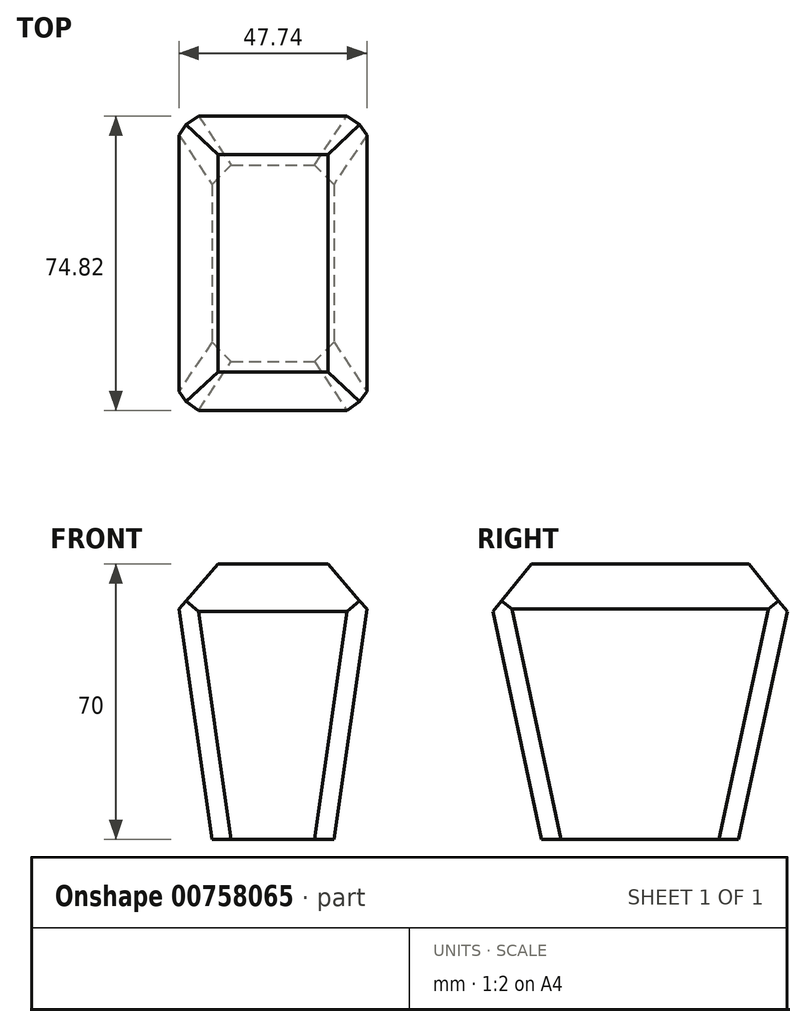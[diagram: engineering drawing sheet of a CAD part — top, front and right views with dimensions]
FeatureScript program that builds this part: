
annotation { "Feature Type Name" : "Feature", "Feature Type Description" : "" }
export const myFeature = defineFeature(function(context is Context, id is Id, definition is map)
    precondition{}
    {
        {
            var Q0;
            Q0=qCreatedBy(makeId("Top.planeOp"),FACE);
            cPlane(context, id + "F0", {"entities" : qUnion([Q0]), "cplaneType" : CPlaneType.OFFSET, "offset" : 70 * mm, "width" : 150 * mm, "height" : 150 * mm});
        }
        {
            var Q0;
            Q0=qCreatedBy(makeId("Top.planeOp"),FACE);
            var sketch = newSketch(context, id + "F1", { "sketchPlane" : qUnion([Q0])});
            skLineSegment(sketch, "E0.bottom", {"start": v(-15.5, 25) * mm, "end": v(15.5, 25) * mm});
            skLineSegment(sketch, "E0.top", {"start": v(-15.5, -25) * mm, "end": v(15.5, -25) * mm});
            skLineSegment(sketch, "E0.left", {"start": v(-15.5, 25) * mm, "end": v(-15.5, -25) * mm});
            skLineSegment(sketch, "E0.right", {"start": v(15.5, 25) * mm, "end": v(15.5, -25) * mm});
            skSolve(sketch);
        }
        {
            var Q0;
            Q0=qCreatedBy(id+"F0.planeOp",FACE);
            var sketch = newSketch(context, id + "F2", { "sketchPlane" : qUnion([Q0])});
            skLineSegment(sketch, "E1.bottom", {"start": v(-25.5, 40) * mm, "end": v(25.5, 40) * mm});
            skLineSegment(sketch, "E1.top", {"start": v(-25.5, -40) * mm, "end": v(25.5, -40) * mm});
            skLineSegment(sketch, "E1.left", {"start": v(-25.5, 40) * mm, "end": v(-25.5, -40) * mm});
            skLineSegment(sketch, "E1.right", {"start": v(25.5, 40) * mm, "end": v(25.5, -40) * mm});
            skSolve(sketch);
        }
        {
            var Q0;
            Q0=makeQuery(id+"F1.imprint","IMPRINT",FACE,{"disambiguationData":[TD([[makeQuery(id+"F1.imprint","IMPRINT",EDGE,{"derivedFrom":sQuery(id+"F1.wireOp",EDGE,"E0.bottom")}),-1.0]])]});
            var Q1;
            Q1=makeQuery(id+"F2.imprint","IMPRINT",FACE,{"disambiguationData":[TD([[makeQuery(id+"F2.imprint","IMPRINT",EDGE,{"derivedFrom":sQuery(id+"F2.wireOp",EDGE,"E1.bottom")}),-1.0]])]});
            loft(context, id + "F3", {"sheetProfilesArray" : [{ "sheetProfileEntities" : qUnion([Q0]) }, { "sheetProfileEntities" : qUnion([Q1]) }]});
        }
        {
            var Q0;
            Q0=makeQuery(id+"F3.opLoft","CAP_FACE",FACE,{"disambiguationData":[OSD([makeQuery(id+"F2.imprint","IMPRINT",FACE,{"disambiguationData":[TD([[makeQuery(id+"F2.imprint","IMPRINT",EDGE,{"derivedFrom":sQuery(id+"F2.wireOp",EDGE,"E1.bottom")}),-1.0]])]})])],"isStart":true});
            chamfer(context, id + "F4", {"entities" : qUnion([Q0]), "width" : 10 * mm, "tangentPropagation" : true});
        }
        {
            var Q0;
            Q0=makeQuery(id+"F3.opLoft","SWEPT_EDGE",EDGE,{"disambiguationData":[OSD([sQuery(id+"F1.wireOp",EDGE,"E0.bottom"),sQuery(id+"F1.wireOp",EDGE,"E0.left"),sQuery(id+"F2.wireOp",EDGE,"E1.bottom"),sQuery(id+"F2.wireOp",EDGE,"E1.left")])]});
            var Q1;
            Q1=makeQuery(id+"F3.opLoft","SWEPT_EDGE",EDGE,{"disambiguationData":[OSD([sQuery(id+"F1.wireOp",EDGE,"E0.top"),sQuery(id+"F1.wireOp",EDGE,"E0.left"),sQuery(id+"F2.wireOp",EDGE,"E1.top"),sQuery(id+"F2.wireOp",EDGE,"E1.left")])]});
            var Q2;
            Q2=makeQuery(id+"F3.opLoft","SWEPT_EDGE",EDGE,{"disambiguationData":[OSD([sQuery(id+"F1.wireOp",EDGE,"E0.top"),sQuery(id+"F1.wireOp",EDGE,"E0.right"),sQuery(id+"F2.wireOp",EDGE,"E1.top"),sQuery(id+"F2.wireOp",EDGE,"E1.right")])]});
            var Q3;
            Q3=makeQuery(id+"F3.opLoft","SWEPT_EDGE",EDGE,{"disambiguationData":[OSD([sQuery(id+"F1.wireOp",EDGE,"E0.bottom"),sQuery(id+"F1.wireOp",EDGE,"E0.right"),sQuery(id+"F2.wireOp",EDGE,"E1.bottom"),sQuery(id+"F2.wireOp",EDGE,"E1.right")])]});
            chamfer(context, id + "F5", {"entities" : qUnion([Q0, Q1, Q2, Q3]), "width" : 5 * mm, "tangentPropagation" : true});
        }
    });
